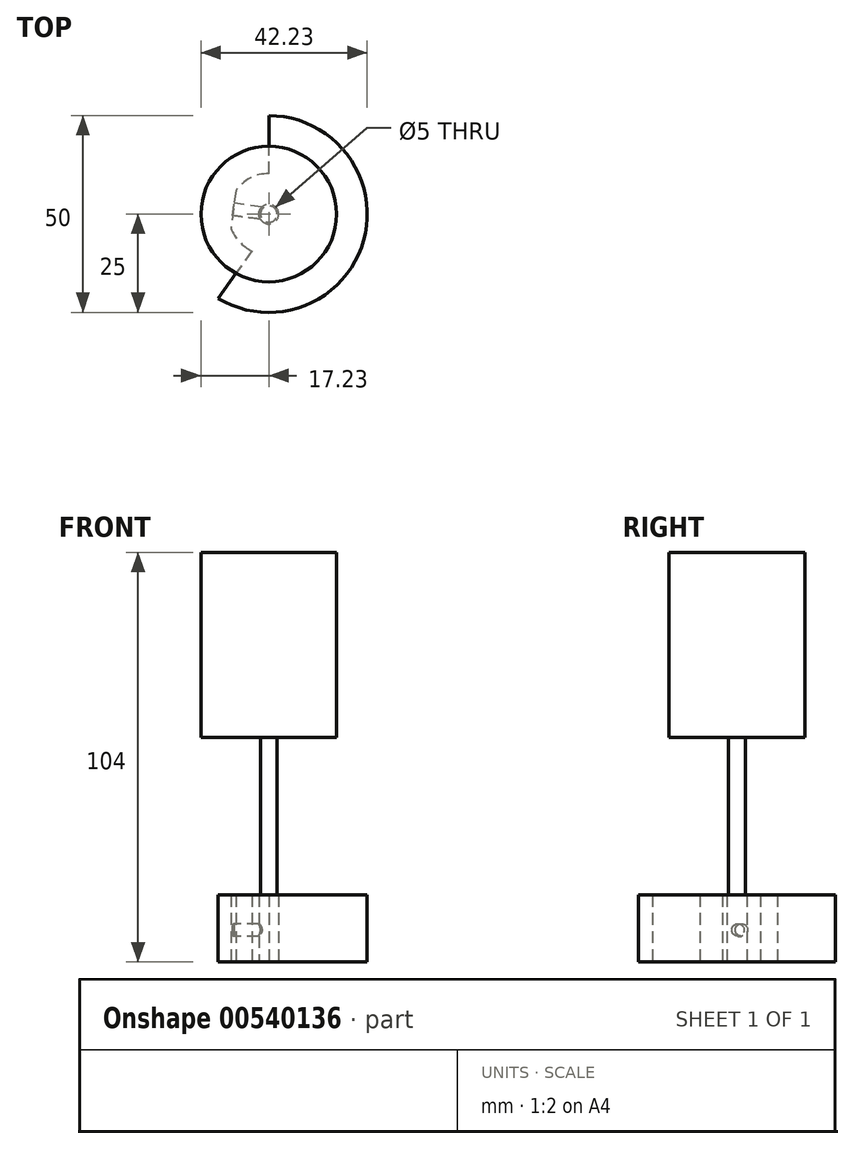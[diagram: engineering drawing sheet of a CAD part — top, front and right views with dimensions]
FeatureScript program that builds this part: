
annotation { "Feature Type Name" : "Feature", "Feature Type Description" : "" }
export const myFeature = defineFeature(function(context is Context, id is Id, definition is map)
    precondition{}
    {
        {
            var Q0;
            Q0=qCreatedBy(makeId("Top.planeOp"),FACE);
            var sketch = newSketch(context, id + "F0", { "sketchPlane" : qUnion([Q0])});
            skArc(sketch, "E0", {"start": v(-12.9, -21.42) * mm, "mid": v(24.09, -6.7) * mm, "end": v(0, 25) * mm});
            skLineSegment(sketch, "E1", {"start": v(0, 10.28) * mm, "end": v(0, 25) * mm});
            skArc(sketch, "E2", {"start": v(0, 10.28) * mm, "mid": v(-4.71, 9.14) * mm, "end": v(-8.38, 5.96) * mm});
            skLineSegment(sketch, "E3", {"start": v(-4.3, -9.34) * mm, "end": v(-12.9, -21.42) * mm});
            skCircle(sketch, "E4", {"center": v(0, 0) * mm, "radius": 2.5 * mm});
            skLineSegment(sketch, "E5", {"start": v(-8.38, 5.96) * mm, "end": v(-9.62, -3.64) * mm});
            skArc(sketch, "E6.trimOffspring", {"start": v(-9.62, -3.64) * mm, "mid": v(-7.52, -7) * mm, "end": v(-4.3, -9.34) * mm});
            skSolve(sketch);
        }
        {
            var Q0;
            {var subQ0=sQuery(id+"F0.wireOp",EDGE,"E0");Q0=makeQuery(id+"F0.imprint","IMPRINT",FACE,{"disambiguationData":[TD([[makeQuery(id+"F0.imprint","IMPRINT",EDGE,{"derivedFrom":subQ0}),1.0]])]});}
            extrude(context, id + "F1", {"entities" : qUnion([Q0]), "depth" : 17 * mm, "offsetDistance" : 25 * mm});
        }
        {
            var Q0;
            Q0=makeQuery(id+"F1.opExtrude","CAP_FACE",FACE,{"disambiguationData":[OSD([sQuery(id+"F0.wireOp",EDGE,"E0"),sQuery(id+"F0.wireOp",EDGE,"E1"),sQuery(id+"F0.wireOp",EDGE,"E2"),sQuery(id+"F0.wireOp",EDGE,"E3"),sQuery(id+"F0.wireOp",EDGE,"E4")])],"isStart":false});
            var sketch = newSketch(context, id + "F2", { "sketchPlane" : qUnion([Q0])});
            skCircle(sketch, "E7", {"center": v(0, 0) * mm, "radius": 2.12 * mm});
            skSolve(sketch);
        }
        {
            var Q0;
            Q0=makeQuery(id+"F2.imprint","IMPRINT",FACE,{"disambiguationData":[TD([[makeQuery(id+"F2.imprint","IMPRINT",EDGE,{"derivedFrom":sQuery(id+"F2.wireOp",EDGE,"E7")}),1.0]])]});
            extrude(context, id + "F3", {"entities" : qUnion([Q0]), "depth" : 40 * mm, "offsetDistance" : 25 * mm});
        }
        {
            var Q0;
            Q0=makeQuery(id+"F3.opExtrude","CAP_FACE",FACE,{"disambiguationData":[OSD([sQuery(id+"F2.wireOp",EDGE,"E7")])],"isStart":false});
            var sketch = newSketch(context, id + "F4", { "sketchPlane" : qUnion([Q0])});
            skCircle(sketch, "E8", {"center": v(0, 0) * mm, "radius": 17.23 * mm});
            skSolve(sketch);
        }
        {
            var Q0;
            Q0=makeQuery(id+"F4.imprint","IMPRINT",FACE,{"disambiguationData":[TD([[makeQuery(id+"F4.imprint","IMPRINT",EDGE,{"derivedFrom":makeQuery(id+"F3.opExtrude","CAP_EDGE",EDGE,{"disambiguationData":[OSD([sQuery(id+"F2.wireOp",EDGE,"E7")])],"isStart":false})}),1.0]])]});
            var Q1;
            Q1=makeQuery(id+"F4.imprint","IMPRINT",FACE,{"disambiguationData":[TD([[makeQuery(id+"F4.imprint","IMPRINT",EDGE,{"derivedFrom":sQuery(id+"F4.wireOp",EDGE,"E8")}),1.0]])]});
            extrude(context, id + "F5", {"entities" : qUnion([Q0, Q1]), "operationType" : NewBodyOperationType.ADD, "depth" : 47 * mm, "offsetDistance" : 25 * mm});
        }
        {
            var Q0;
            Q0=makeQuery(id+"F1.opExtrude","SWEPT_FACE",FACE,{"disambiguationData":[OSD([sQuery(id+"F0.wireOp",EDGE,"E5")])]});
            var sketch = newSketch(context, id + "F6", { "sketchPlane" : qUnion([Q0])});
            skCircle(sketch, "E9", {"center": v(0, 8.11) * mm, "radius": 1.58 * mm});
            skSolve(sketch);
        }
        {
            var Q0;
            Q0=makeQuery(id+"F6.imprint","IMPRINT",FACE,{"disambiguationData":[TD([[makeQuery(id+"F6.imprint","IMPRINT",EDGE,{"derivedFrom":sQuery(id+"F6.wireOp",EDGE,"E9")}),1.0]])]});
            extrude(context, id + "F7", {"entities" : qUnion([Q0]), "operationType" : NewBodyOperationType.REMOVE, "endBound" : BoundingType.UP_TO_NEXT, "oppositeDirection" : true, "depth" : 25 * mm, "offsetDistance" : 25 * mm});
        }
    });
